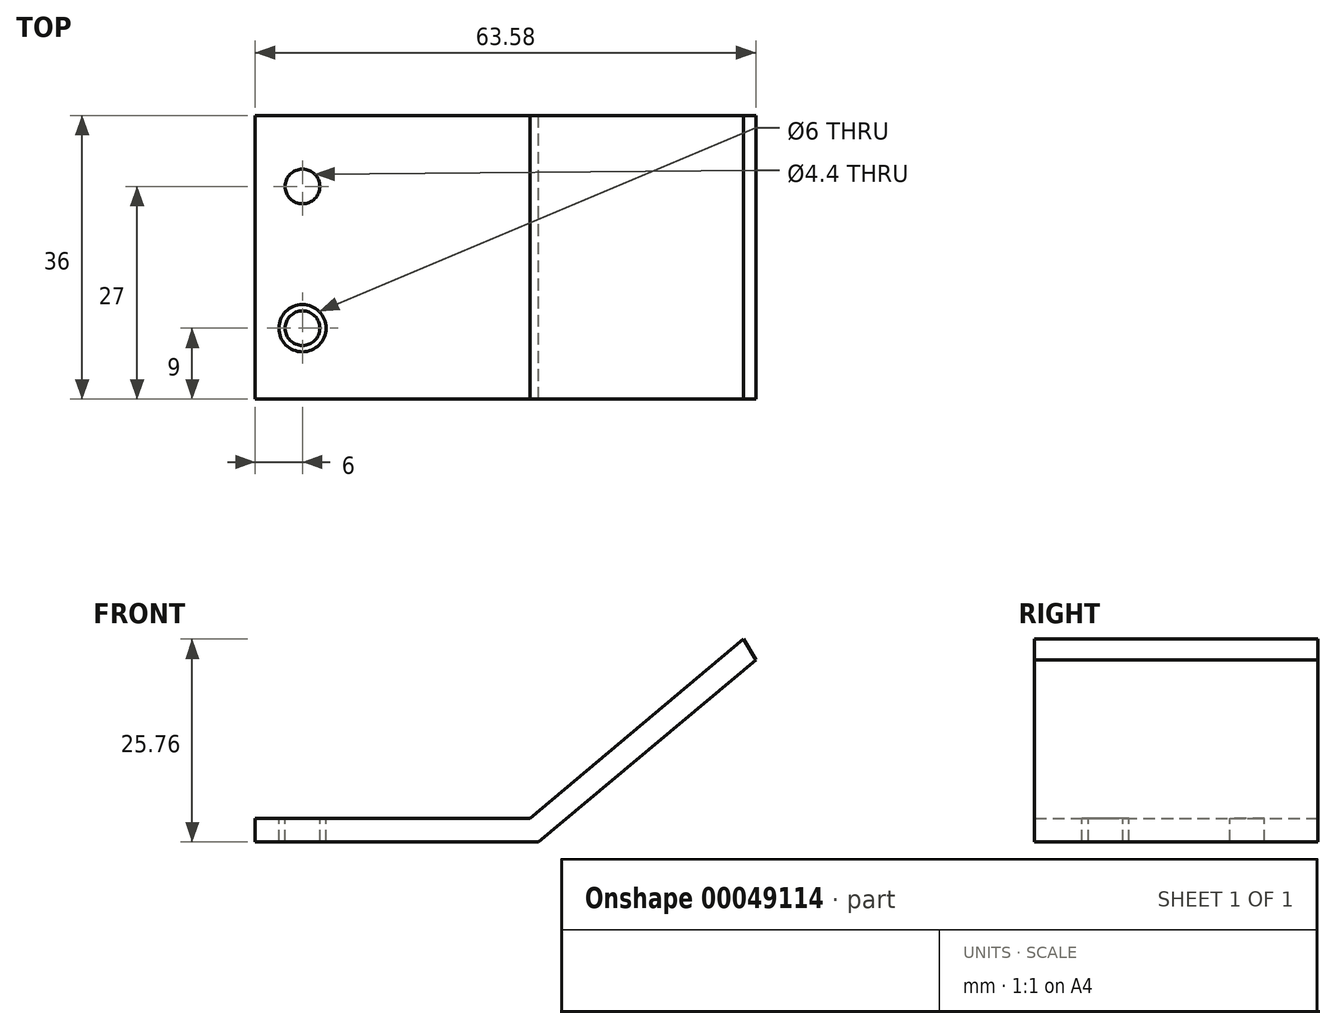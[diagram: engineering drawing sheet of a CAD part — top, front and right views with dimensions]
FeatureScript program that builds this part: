
annotation { "Feature Type Name" : "Feature", "Feature Type Description" : "" }
export const myFeature = defineFeature(function(context is Context, id is Id, definition is map)
    precondition{}
    {
        {
            var Q0;
            Q0=qCreatedBy(makeId("Front.planeOp"),FACE);
            var sketch = newSketch(context, id + "F0", { "sketchPlane" : qUnion([Q0])});
            skLineSegment(sketch, "E0", {"start": v(0, 0) * mm, "end": v(-36, 0) * mm});
            skLineSegment(sketch, "E1", {"start": v(0, 0) * mm, "end": v(27.58, 23.14) * mm});
            skLineSegment(sketch, "E2.0", {"start": v(-1.1, 3) * mm, "end": v(-36, 3) * mm});
            skLineSegment(sketch, "E2.1", {"start": v(-1.1, 3) * mm, "end": v(26.03, 25.76) * mm});
            skLineSegment(sketch, "E3", {"start": v(-36, 0) * mm, "end": v(-36, 3) * mm});
            skLineSegment(sketch, "E4", {"start": v(27.58, 23.14) * mm, "end": v(26.03, 25.76) * mm});
            skSolve(sketch);
        }
        {
            var Q0;
            Q0=makeQuery(id+"F0.imprint","IMPRINT",FACE,{"disambiguationData":[TD([[makeQuery(id+"F0.imprint","IMPRINT",EDGE,{"derivedFrom":sQuery(id+"F0.wireOp",EDGE,"E0")}),-1.0]])]});
            extrude(context, id + "F1", {"entities" : qUnion([Q0]), "depth" : 36 * mm});
        }
        {
            var Q0;
            Q0=makeQuery(id+"F1.opExtrude","SWEPT_FACE",FACE,{"disambiguationData":[OSD([sQuery(id+"F0.wireOp",EDGE,"E2.0")])]});
            var sketch = newSketch(context, id + "F2", { "sketchPlane" : qUnion([Q0])});
            skLineSegment(sketch, "E5", {"start": v(-30, -36) * mm, "end": v(-30, 0) * mm, "construction": true});
            skCircle(sketch, "E6", {"center": v(-30, -9) * mm, "radius": 3 * mm});
            skCircle(sketch, "E7", {"center": v(-30, -9) * mm, "radius": 2.2 * mm});
            skLineSegment(sketch, "E8", {"start": v(-36, -18) * mm, "end": v(-1.1, -18) * mm, "construction": true});
            skCircle(sketch, "E9.MirrorC", {"center": v(-30, -27) * mm, "radius": 3 * mm});
            skCircle(sketch, "E10.MirrorC", {"center": v(-30, -27) * mm, "radius": 2.2 * mm});
            skSolve(sketch);
        }
        {
            var Q0;
            Q0=makeQuery(id+"F2.imprint","IMPRINT",FACE,{"disambiguationData":[TD([[makeQuery(id+"F2.imprint","IMPRINT",EDGE,{"derivedFrom":sQuery(id+"F2.wireOp",EDGE,"E7")}),1.0]])]});
            var Q1;
            Q1=makeQuery(id+"F2.imprint","IMPRINT",FACE,{"disambiguationData":[TD([[makeQuery(id+"F2.imprint","IMPRINT",EDGE,{"derivedFrom":sQuery(id+"F2.wireOp",EDGE,"E10.MirrorC")}),-1.0]])]});
            extrude(context, id + "F3", {"entities" : qUnion([Q0, Q1]), "operationType" : NewBodyOperationType.REMOVE, "endBound" : BoundingType.THROUGH_ALL, "oppositeDirection" : true, "depth" : 25 * mm});
        }
    });
